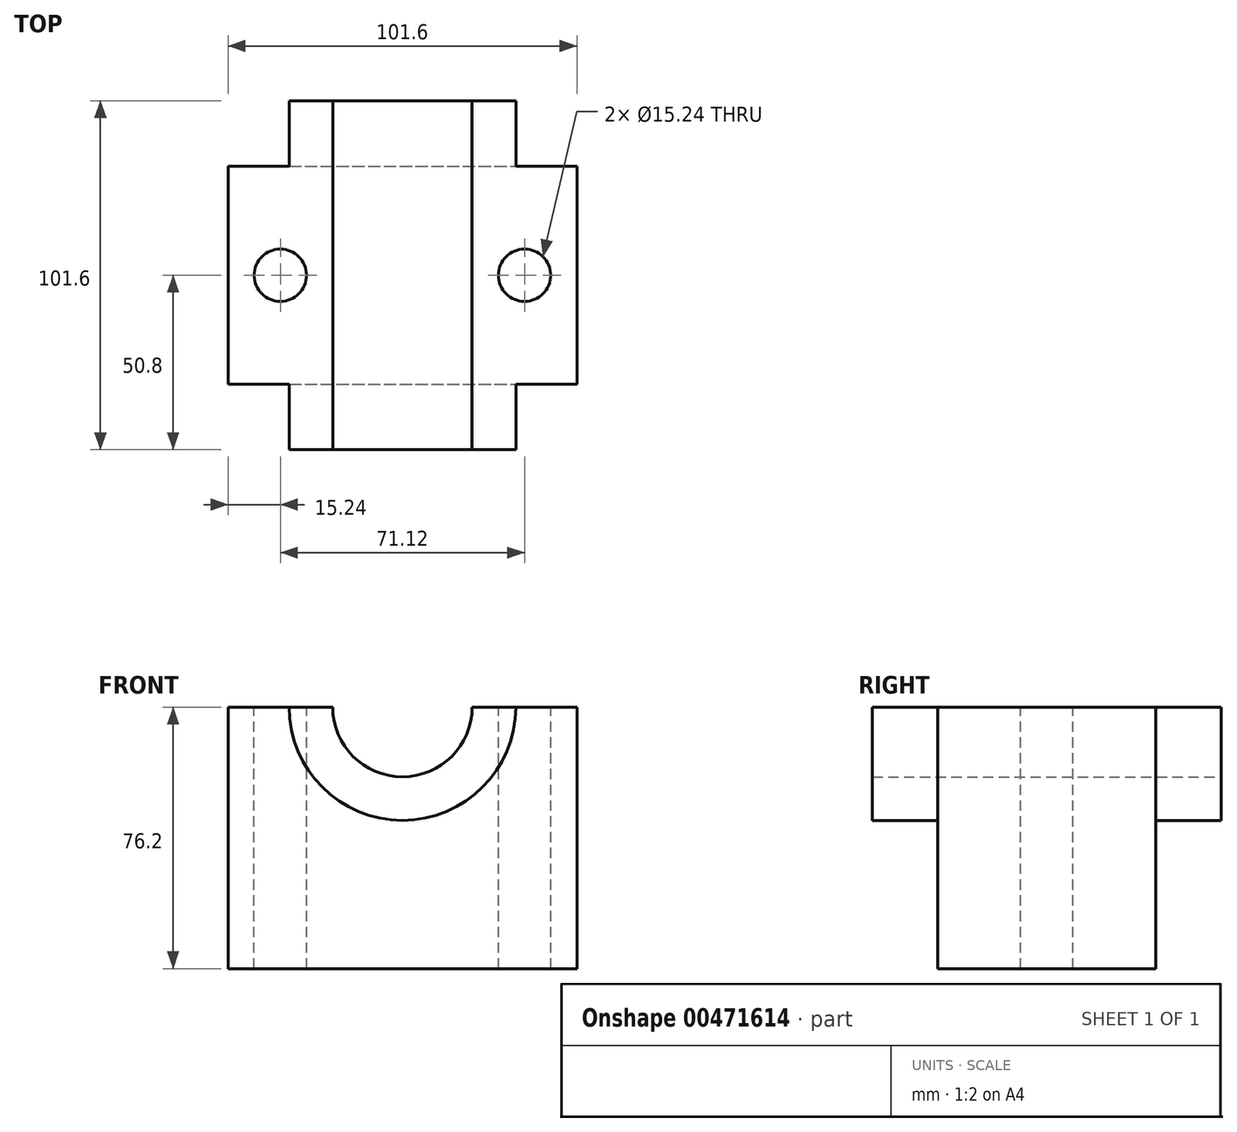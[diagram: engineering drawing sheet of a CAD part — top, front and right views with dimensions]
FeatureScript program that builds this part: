
annotation { "Feature Type Name" : "Feature", "Feature Type Description" : "" }
export const myFeature = defineFeature(function(context is Context, id is Id, definition is map)
    precondition{}
    {
        {
            var Q0;
            Q0=qCreatedBy(makeId("Front.planeOp"),FACE);
            var sketch = newSketch(context, id + "F0", { "sketchPlane" : qUnion([Q0])});
            skLineSegment(sketch, "E0.bottom", {"start": v(-50.8, 38.1) * mm, "end": v(50.8, 38.1) * mm});
            skLineSegment(sketch, "E0.top", {"start": v(-50.8, -38.1) * mm, "end": v(50.8, -38.1) * mm});
            skLineSegment(sketch, "E0.left", {"start": v(-50.8, 38.1) * mm, "end": v(-50.8, -38.1) * mm});
            skLineSegment(sketch, "E0.right", {"start": v(50.8, 38.1) * mm, "end": v(50.8, -38.1) * mm});
            skSolve(sketch);
        }
        {
            var Q0;
            Q0 = qSketchRegion(id + "F0", true);
            extrude(context, id + "F1", {"entities" : qUnion([Q0]), "endBound" : BoundingType.SYMMETRIC, "depth" : 63.5 * mm});
        }
        {
            var Q0;
            Q0=qCreatedBy(makeId("Front.planeOp"),FACE);
            var sketch = newSketch(context, id + "F2", { "sketchPlane" : qUnion([Q0])});
            skArc(sketch, "E1", {"start": v(-20.32, 38.1) * mm, "mid": v(0, 17.78) * mm, "end": v(20.32, 38.1) * mm});
            skLineSegment(sketch, "E2", {"start": v(0, 53.84) * mm, "end": v(0, -62.26) * mm, "construction": true});
            skArc(sketch, "E3.0", {"start": v(-33.02, 38.1) * mm, "mid": v(0, 5.08) * mm, "end": v(33.02, 38.1) * mm});
            skLineSegment(sketch, "E4", {"start": v(-33.02, 38.1) * mm, "end": v(-20.32, 38.1) * mm});
            skLineSegment(sketch, "E5", {"start": v(20.32, 38.1) * mm, "end": v(33.02, 38.1) * mm});
            skSolve(sketch);
        }
        {
            var Q0;
            Q0 = qSketchRegion(id + "F2", true);
            extrude(context, id + "F3", {"entities" : qUnion([Q0]), "operationType" : NewBodyOperationType.ADD, "endBound" : BoundingType.SYMMETRIC, "depth" : 101.6 * mm});
        }
        {
            var Q0;
            {var subQ0=sQuery(id+"F0.wireOp",EDGE,"E0.bottom");Q0=makeQuery(id+"F3.boolean.opBoolean","SPLIT",FACE,{"disambiguationData":[TD([makeQuery(id+"F3.opExtrude","SWEPT_FACE",FACE,{"disambiguationData":[OSD([sQuery(id+"F2.wireOp",EDGE,"E1")])]})])],"derivedFrom":makeQuery(id+"F1.opExtrude","CAP_FACE",FACE,{"disambiguationData":[OSD([subQ0,sQuery(id+"F0.wireOp",EDGE,"E0.top"),sQuery(id+"F0.wireOp",EDGE,"E0.left"),sQuery(id+"F0.wireOp",EDGE,"E0.right")])],"isStart":false})});}
            var sketch = newSketch(context, id + "F4", { "sketchPlane" : qUnion([Q0])});
            skSolve(sketch);
        }
        {
            var Q0;
            {var subQ0=sQuery(id+"F0.wireOp",EDGE,"E0.bottom");var subQ1=makeQuery(id+"F1.opExtrude","CAP_FACE",FACE,{"disambiguationData":[OSD([subQ0,sQuery(id+"F0.wireOp",EDGE,"E0.top"),sQuery(id+"F0.wireOp",EDGE,"E0.left"),sQuery(id+"F0.wireOp",EDGE,"E0.right")])],"isStart":false});var subQ2=makeQuery(id+"F3.opExtrude","SWEPT_FACE",FACE,{"disambiguationData":[OSD([sQuery(id+"F2.wireOp",EDGE,"E1")])]});Q0=makeQuery(id+"F4.imprint","IMPRINT",FACE,{"disambiguationData":[TD([[makeQuery(id+"F4.imprint","IMPRINT",EDGE,{"derivedFrom":makeQuery(id+"F3.boolean.opBoolean","INTERSECT",EDGE,{"derivedFrom":[subQ1,subQ2]})}),-1.0]])]});}
            extrude(context, id + "F5", {"entities" : qUnion([Q0]), "operationType" : NewBodyOperationType.REMOVE, "oppositeDirection" : true, "depth" : 76.2 * mm});
        }
        {
            var Q0;
            {var subQ1=sQuery(id+"F0.wireOp",EDGE,"E0.right");var subQ4=sQuery(id+"F0.wireOp",EDGE,"E0.bottom");var subQ6=sQuery(id+"F2.wireOp",EDGE,"E5");var subQ7=sQuery(id+"F2.wireOp",EDGE,"E4");Q0=makeQuery(id+"F5.boolean.opBoolean","SPLIT",FACE,{"disambiguationData":[TD([makeQuery(id+"F1.opExtrude","SWEPT_FACE",FACE,{"disambiguationData":[OSD([subQ1])]})])],"derivedFrom":makeQuery(id+"F3.boolean.opBoolean","MERGE",FACE,{"derivedFrom":[makeQuery(id+"F1.opExtrude","SWEPT_FACE",FACE,{"disambiguationData":[OSD([subQ4])]}),makeQuery(id+"F3.opExtrude","SWEPT_FACE",FACE,{"disambiguationData":[OSD([subQ7])]}),makeQuery(id+"F3.opExtrude","SWEPT_FACE",FACE,{"disambiguationData":[OSD([subQ6])]})]})});}
            var sketch = newSketch(context, id + "F6", { "sketchPlane" : qUnion([Q0])});
            skCircle(sketch, "E6", {"center": v(-35.56, 0) * mm, "radius": 7.62 * mm});
            skLineSegment(sketch, "E7", {"start": v(0, -93.78) * mm, "end": v(0, 94.83) * mm, "construction": true});
            skCircle(sketch, "E8.MirrorC", {"center": v(35.56, 0) * mm, "radius": 7.62 * mm});
            skSolve(sketch);
        }
        {
            var Q0;
            Q0 = qSketchRegion(id + "F6", true);
            extrude(context, id + "F7", {"entities" : qUnion([Q0]), "operationType" : NewBodyOperationType.REMOVE, "oppositeDirection" : true, "depth" : 76.2 * mm});
        }
    });
